# Revit family: PlumbingFixture_GroheLimited_SwitchPowerSupply_36338000_METRIC1
name_source: partatom
category: Plumbing Fixtures
revit_build: Autodesk Revit 2015 (Build: 20160512_1515(x64)
units: mm (PartAtom-declared; Revit-internal decimal feet)

## types (1)
- 36338000
    ADACompliant = No
    Assembly Code = D2010
    AssetType = Fixed
    BIMObjectName = PlumbingFixture_GroheLimited_SwitchPowerSupply_36338000_METRIC
    CW Connection = No
    CWFU = 4.5
    ClassificationName = Uniclass2015
    ClassificationValue = Pr_40_20_93_79
    ColdWaterConnectionDiameter = 10 mm  [stored 0.0328084 ft]
    Color = Cream
    Cost = 0 $
    Default Elevation = 0 mm  [stored 0 ft]
    Description = for one eye infra-red wash basin mixer. switch mode power supply with operating voltage. 100-230 V AC, 50 - 60 Hz. for concealed socket with cover and strain relief. can be used by the following products: 36 095 000, 36 097 000, 36 088 000, 36 091 000, 36 411 000, 36 413 000, 36 409 000, 36 325 001, 36 269 000 , 36015001 , 36016001 , 36421000
    DurationUnit = Years
    Ecojoy = No
    ExpectedLife = 0
    Features = for one eye infra-red wash basin mixer. switch mode power supply with operating voltage. 100-230 V AC, 50 - 60 Hz. for concealed socket with cover and strain relief. can be used by the following products: 36 095 000, 36 097 000, 36 088 000, 36 091 000, 36 411 000, 36 413 000, 36 409 000, 36 325 001, 36 269 000 , 36015001 , 36016001 , 36421000
    Finish = Plastic
    HW Connection = No
    HWFU = 4.5
    HotWaterConnectionDiameter = 10 mm  [stored 0.0328084 ft]
    IfcExportAs = IfcPipeFitting
    IfcExportType = IfcPipeFittingType
    Keynote = N13
    LowEmittingMaterial = No
    Manufacturer = Grohe Limited
    ManufacturerName = Grohe Limited
    MasterformatNumber = 01 52 19
    MasterformatTitle = Sanitary Facilities
    Material = Plastic
    Model = Switch mode power supply
    ModelNumber = 36338000
    ModelReference = Switch mode power supply
    NBSDescription = Urinal flushing valves
    NBSObjectName = Grohe Limited - Urinal flushing valves
    NBSReference = 45-35-70/355
    NominalDepth = 0 mm  [stored 0 ft]
    NominalHeight = 0 mm  [stored 0 ft]
    NominalLength = 0 mm  [stored 0 ft]
    ProductDocumentationLink = https://www.grohe.co.uk
    ProductPageURL = https://www.grohe.co.uk
    ProductionYear = 2017
    Type Comments = 36338000
    TypeName = Switch mode power supply
    URL = www.grohe.com
    Vent Connection = No
    WFU = 0
    WarrantyDurationUnit = Years
    Waste Connection = No
    _BSBibleVersion = 14
    _BimSpecGuid = 0
    _CurrentRevision = 1
    _DistributedBy = www.bimstore.co.uk

note: [stored X ft] marks values corroborated as IEEE doubles in the binary element streams (Revit-internal decimal feet)

## geometry (parser evidence)
native form markers: Sweep x2
no freeform markers — native parametric forms only
